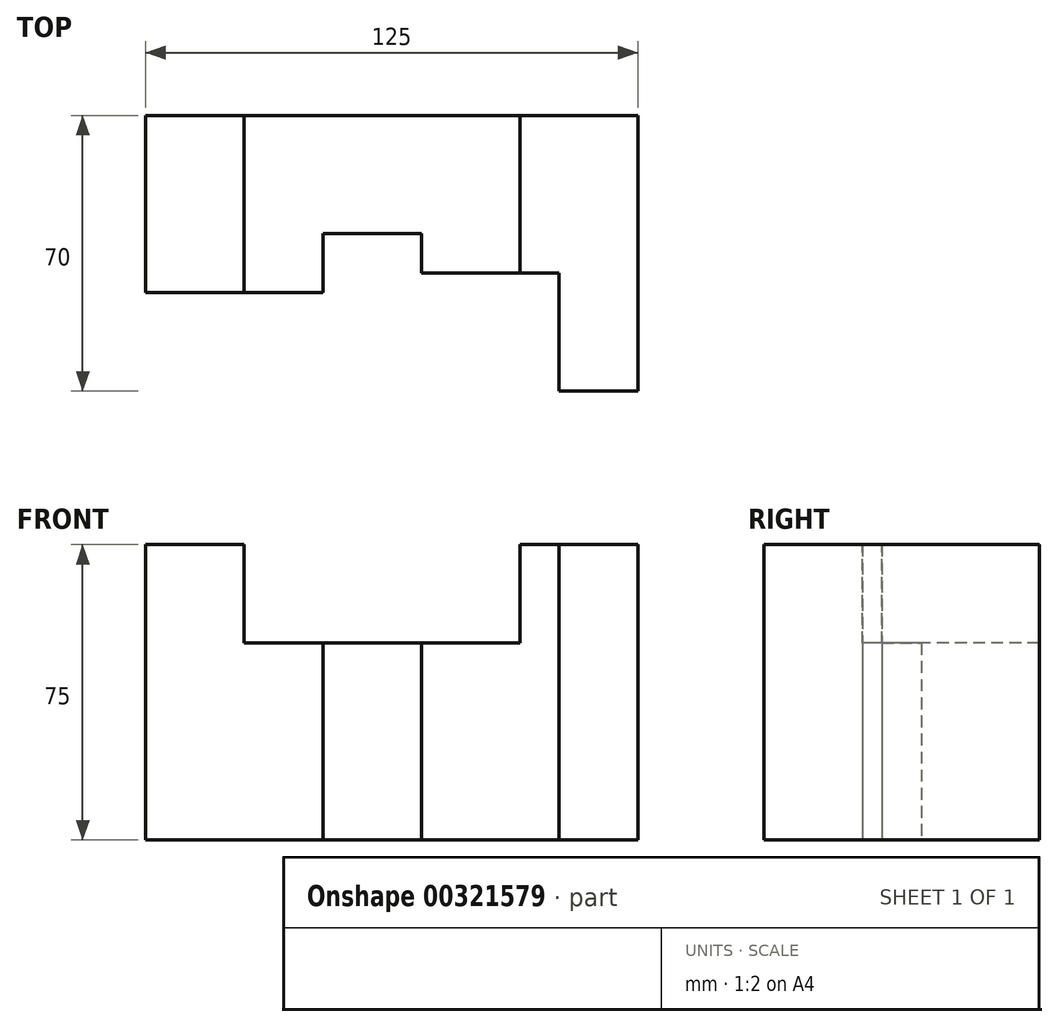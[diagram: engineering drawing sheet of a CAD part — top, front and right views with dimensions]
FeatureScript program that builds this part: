
annotation { "Feature Type Name" : "Feature", "Feature Type Description" : "" }
export const myFeature = defineFeature(function(context is Context, id is Id, definition is map)
    precondition{}
    {
        {
            var Q0;
            Q0=qCreatedBy(makeId("Front.planeOp"),FACE);
            var sketch = newSketch(context, id + "F0", { "sketchPlane" : qUnion([Q0])});
            skLineSegment(sketch, "E0.bottom", {"start": v(0, 0) * mm, "end": v(125, 0) * mm});
            skLineSegment(sketch, "E0.top", {"start": v(0, 75) * mm, "end": v(125, 75) * mm});
            skLineSegment(sketch, "E0.left", {"start": v(0, 0) * mm, "end": v(0, 75) * mm});
            skLineSegment(sketch, "E0.right", {"start": v(125, 0) * mm, "end": v(125, 75) * mm});
            skSolve(sketch);
        }
        {
            var Q0;
            Q0 = qSketchRegion(id + "F0", true);
            extrude(context, id + "F1", {"entities" : qUnion([Q0]), "depth" : 70 * mm});
        }
        {
            var Q0;
            Q0=makeQuery(id+"F1.opExtrude","CAP_FACE",FACE,{"disambiguationData":[OSD([sQuery(id+"F0.wireOp",EDGE,"E0.bottom"),sQuery(id+"F0.wireOp",EDGE,"E0.top"),sQuery(id+"F0.wireOp",EDGE,"E0.left"),sQuery(id+"F0.wireOp",EDGE,"E0.right")])],"isStart":false});
            var sketch = newSketch(context, id + "F2", { "sketchPlane" : qUnion([Q0])});
            skLineSegment(sketch, "E1.bottom", {"start": v(25, 75) * mm, "end": v(95, 75) * mm});
            skLineSegment(sketch, "E1.top", {"start": v(25, 50) * mm, "end": v(95, 50) * mm});
            skLineSegment(sketch, "E1.left", {"start": v(25, 75) * mm, "end": v(25, 50) * mm});
            skLineSegment(sketch, "E1.right", {"start": v(95, 75) * mm, "end": v(95, 50) * mm});
            skSolve(sketch);
        }
        {
            var Q0;
            Q0 = qSketchRegion(id + "F2", true);
            extrude(context, id + "F3", {"entities" : qUnion([Q0]), "operationType" : NewBodyOperationType.REMOVE, "endBound" : BoundingType.THROUGH_ALL, "oppositeDirection" : true, "depth" : 25 * mm});
        }
        {
            var Q0;
            Q0=qCreatedBy(makeId("Top.planeOp"),FACE);
            var sketch = newSketch(context, id + "F4", { "sketchPlane" : qUnion([Q0])});
            skLineSegment(sketch, "E2", {"start": v(105, -70) * mm, "end": v(105, -40) * mm});
            skLineSegment(sketch, "E3", {"start": v(105, -40) * mm, "end": v(70, -40) * mm});
            skLineSegment(sketch, "E4", {"start": v(70, -40) * mm, "end": v(70, -30) * mm});
            skLineSegment(sketch, "E5", {"start": v(70, -30) * mm, "end": v(45, -30) * mm});
            skLineSegment(sketch, "E6", {"start": v(45, -30) * mm, "end": v(45, -45) * mm});
            skLineSegment(sketch, "E7", {"start": v(45, -45) * mm, "end": v(0, -45) * mm});
            skLineSegment(sketch, "E8", {"start": v(0, -45) * mm, "end": v(0, -118.38) * mm});
            skLineSegment(sketch, "E9", {"start": v(0, -118.38) * mm, "end": v(105, -118.38) * mm});
            skLineSegment(sketch, "E10", {"start": v(105, -118.38) * mm, "end": v(105, -70) * mm});
            skSolve(sketch);
        }
        {
            var Q0;
            Q0 = qSketchRegion(id + "F4", true);
            extrude(context, id + "F5", {"entities" : qUnion([Q0]), "operationType" : NewBodyOperationType.REMOVE, "endBound" : BoundingType.THROUGH_ALL, "depth" : 25 * mm});
        }
    });
